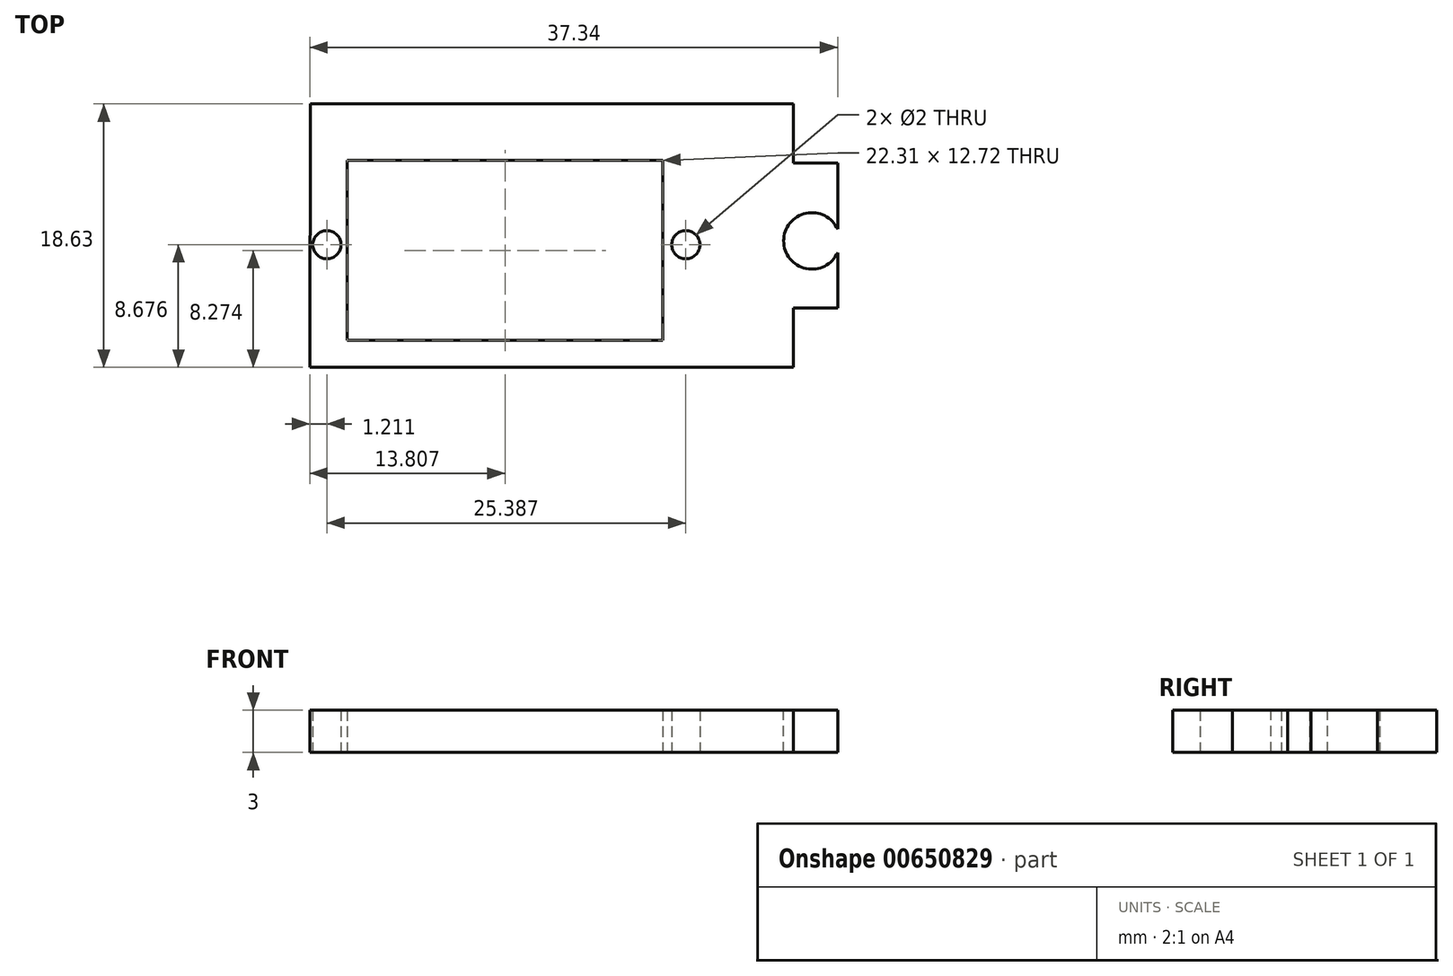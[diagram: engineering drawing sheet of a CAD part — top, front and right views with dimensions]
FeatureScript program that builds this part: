
annotation { "Feature Type Name" : "Feature", "Feature Type Description" : "" }
export const myFeature = defineFeature(function(context is Context, id is Id, definition is map)
    precondition{}
    {
        {
            var Q0;
            Q0=qCreatedBy(makeId("Top.planeOp"),FACE);
            var sketch = newSketch(context, id + "F0", { "sketchPlane" : qUnion([Q0])});
            skLineSegment(sketch, "E0", {"start": v(-63.28, 54.77) * mm, "end": v(-29.12, 54.77) * mm});
            skLineSegment(sketch, "E1", {"start": v(-60.66, 50.77) * mm, "end": v(-38.35, 50.77) * mm});
            skLineSegment(sketch, "E2", {"start": v(-38.35, 50.77) * mm, "end": v(-38.35, 38.05) * mm});
            skLineSegment(sketch, "E3", {"start": v(-38.35, 38.05) * mm, "end": v(-60.66, 38.05) * mm});
            skLineSegment(sketch, "E4", {"start": v(-60.66, 38.05) * mm, "end": v(-60.66, 50.77) * mm});
            skLineSegment(sketch, "E5", {"start": v(-29.12, 54.77) * mm, "end": v(-29.12, 50.6) * mm});
            skLineSegment(sketch, "E6", {"start": v(-29.12, 50.6) * mm, "end": v(-25.97, 50.6) * mm});
            skLineSegment(sketch, "E7", {"start": v(-25.97, 50.6) * mm, "end": v(-25.97, 40.33) * mm});
            skLineSegment(sketch, "E8", {"start": v(-25.97, 40.33) * mm, "end": v(-29.12, 40.33) * mm});
            skLineSegment(sketch, "E9", {"start": v(-29.12, 40.33) * mm, "end": v(-29.12, 36.14) * mm});
            skLineSegment(sketch, "E10", {"start": v(-29.12, 36.14) * mm, "end": v(-63.3, 36.14) * mm});
            skLineSegment(sketch, "E11", {"start": v(-63.3, 36.14) * mm, "end": v(-63.28, 54.77) * mm});
            skCircle(sketch, "E12", {"center": v(-29.12, 45.47) * mm, "radius": 1.7 * mm});
            skPoint(sketch, "E12.centerSnap0", {"position": v(-25.97, 45.47) * mm});
            skCircle(sketch, "E13", {"center": v(-36.71, 44.82) * mm, "radius": 0.63 * mm});
            skCircle(sketch, "E14", {"center": v(-62.1, 44.82) * mm, "radius": 1.12 * mm});
            skSolve(sketch);
        }
        {
            var Q0;
            Q0=makeQuery(id+"F0.imprint","IMPRINT",FACE,{"disambiguationData":[TD([[makeQuery(id+"F0.imprint","IMPRINT",EDGE,{"derivedFrom":sQuery(id+"F0.wireOp",EDGE,"E12")}),1.0]])]});
            var Q1;
            Q1=makeQuery(id+"F0.imprint","IMPRINT",FACE,{"disambiguationData":[TD([[makeQuery(id+"F0.imprint","IMPRINT",EDGE,{"derivedFrom":sQuery(id+"F0.wireOp",EDGE,"E14")}),1.0]])]});
            var Q2;
            Q2=makeQuery(id+"F0.imprint","IMPRINT",FACE,{"disambiguationData":[TD([[makeQuery(id+"F0.imprint","IMPRINT",EDGE,{"derivedFrom":sQuery(id+"F0.wireOp",EDGE,"E0")}),-1.0]])]});
            var Q3;
            Q3=makeQuery(id+"F0.imprint","IMPRINT",FACE,{"disambiguationData":[TD([[makeQuery(id+"F0.imprint","IMPRINT",EDGE,{"derivedFrom":sQuery(id+"F0.wireOp",EDGE,"E13")}),1.0]])]});
            extrude(context, id + "F1", {"entities" : qUnion([Q0, Q1, Q2, Q3]), "depth" : 3 * mm, "offsetDistance" : 25 * mm});
        }
        {
            var Q0;
            Q0=sQuery(id+"F0.wireOp",VERTEX,"E14.center");
            var Q1;
            Q1=makeQuery(id+"F1.opExtrude","SWEPT_BODY",BODY,{"disambiguationData":[OSD([sQuery(id+"F0.wireOp",EDGE,"E0"),sQuery(id+"F0.wireOp",EDGE,"E1"),sQuery(id+"F0.wireOp",EDGE,"E2"),sQuery(id+"F0.wireOp",EDGE,"E3"),sQuery(id+"F0.wireOp",EDGE,"E4"),sQuery(id+"F0.wireOp",EDGE,"E5"),sQuery(id+"F0.wireOp",EDGE,"E6"),sQuery(id+"F0.wireOp",EDGE,"E7"),sQuery(id+"F0.wireOp",EDGE,"E8"),sQuery(id+"F0.wireOp",EDGE,"E9"),sQuery(id+"F0.wireOp",EDGE,"E10"),sQuery(id+"F0.wireOp",EDGE,"E11")])]});
            hole(context, id + "F2", {"style" : HoleStyle.SIMPLE, "endStyle" : HoleEndStyle.THROUGH, "oppositeDirection" : true, "holeDiameter" : 2 * mm, "majorDiameter" : 5 * mm, "isTappedThrough" : true, "tappedDepth" : 12 * mm, "tapClearance" : 3, "locations" : qUnion([Q0]), "scope" : qUnion([Q1])});
        }
        {
            var Q0;
            Q0=sQuery(id+"F0.wireOp",VERTEX,"E13.center");
            var Q1;
            Q1=makeQuery(id+"F1.opExtrude","SWEPT_BODY",BODY,{"disambiguationData":[OSD([sQuery(id+"F0.wireOp",EDGE,"E0"),sQuery(id+"F0.wireOp",EDGE,"E1"),sQuery(id+"F0.wireOp",EDGE,"E2"),sQuery(id+"F0.wireOp",EDGE,"E3"),sQuery(id+"F0.wireOp",EDGE,"E4"),sQuery(id+"F0.wireOp",EDGE,"E5"),sQuery(id+"F0.wireOp",EDGE,"E6"),sQuery(id+"F0.wireOp",EDGE,"E7"),sQuery(id+"F0.wireOp",EDGE,"E8"),sQuery(id+"F0.wireOp",EDGE,"E9"),sQuery(id+"F0.wireOp",EDGE,"E10"),sQuery(id+"F0.wireOp",EDGE,"E11")])]});
            hole(context, id + "F3", {"style" : HoleStyle.SIMPLE, "endStyle" : HoleEndStyle.THROUGH, "oppositeDirection" : true, "holeDiameter" : 2 * mm, "majorDiameter" : 5 * mm, "isTappedThrough" : true, "tappedDepth" : 12 * mm, "tapClearance" : 3, "locations" : qUnion([Q0]), "scope" : qUnion([Q1])});
        }
        {
            var Q0;
            Q0=makeQuery(id+"F1.opExtrude","CAP_FACE",FACE,{"disambiguationData":[OSD([sQuery(id+"F0.wireOp",EDGE,"E0"),sQuery(id+"F0.wireOp",EDGE,"E1"),sQuery(id+"F0.wireOp",EDGE,"E2"),sQuery(id+"F0.wireOp",EDGE,"E3"),sQuery(id+"F0.wireOp",EDGE,"E4"),sQuery(id+"F0.wireOp",EDGE,"E5"),sQuery(id+"F0.wireOp",EDGE,"E6"),sQuery(id+"F0.wireOp",EDGE,"E7"),sQuery(id+"F0.wireOp",EDGE,"E8"),sQuery(id+"F0.wireOp",EDGE,"E9"),sQuery(id+"F0.wireOp",EDGE,"E10"),sQuery(id+"F0.wireOp",EDGE,"E11")])],"isStart":false});
            var sketch = newSketch(context, id + "F4", { "sketchPlane" : qUnion([Q0])});
            skCircle(sketch, "E15", {"center": v(-27.8, 45.08) * mm, "radius": 2 * mm});
            skSolve(sketch);
        }
        {
            var Q0;
            Q0=sQuery(id+"F4.wireOp",VERTEX,"E15.center");
            var Q1;
            Q1=makeQuery(id+"F1.opExtrude","SWEPT_BODY",BODY,{"disambiguationData":[OSD([sQuery(id+"F0.wireOp",EDGE,"E0"),sQuery(id+"F0.wireOp",EDGE,"E1"),sQuery(id+"F0.wireOp",EDGE,"E2"),sQuery(id+"F0.wireOp",EDGE,"E3"),sQuery(id+"F0.wireOp",EDGE,"E4"),sQuery(id+"F0.wireOp",EDGE,"E5"),sQuery(id+"F0.wireOp",EDGE,"E6"),sQuery(id+"F0.wireOp",EDGE,"E7"),sQuery(id+"F0.wireOp",EDGE,"E8"),sQuery(id+"F0.wireOp",EDGE,"E9"),sQuery(id+"F0.wireOp",EDGE,"E10"),sQuery(id+"F0.wireOp",EDGE,"E11")])]});
            hole(context, id + "F5", {"style" : HoleStyle.SIMPLE, "endStyle" : HoleEndStyle.THROUGH, "holeDiameter" : 4 * mm, "majorDiameter" : 5 * mm, "isTappedThrough" : true, "tappedDepth" : 12 * mm, "tapClearance" : 3, "locations" : qUnion([Q0]), "scope" : qUnion([Q1])});
        }
    });
